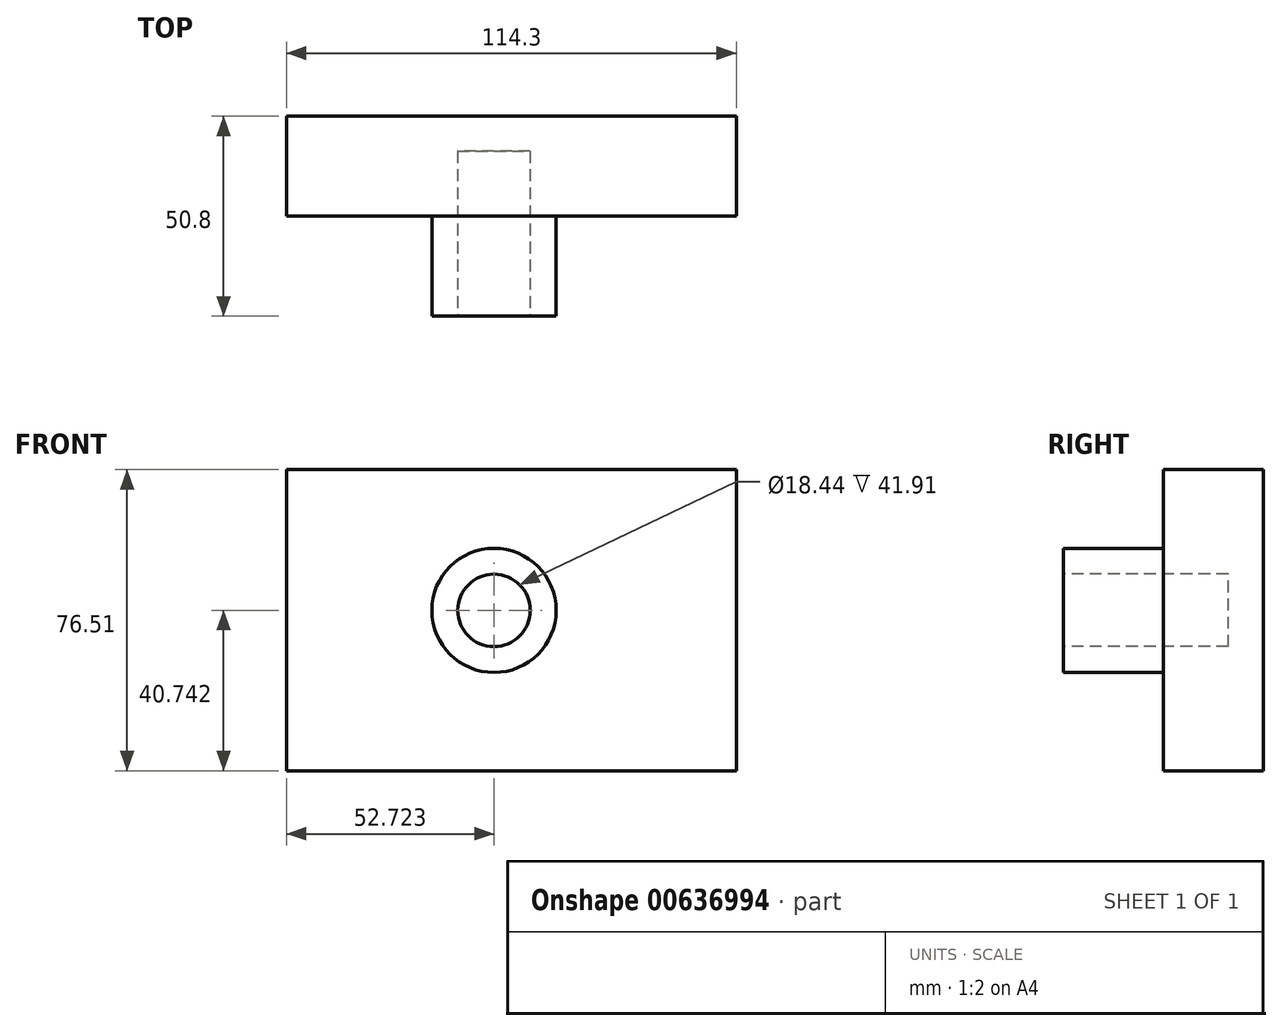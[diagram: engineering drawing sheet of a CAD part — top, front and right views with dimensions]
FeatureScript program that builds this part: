
annotation { "Feature Type Name" : "Feature", "Feature Type Description" : "" }
export const myFeature = defineFeature(function(context is Context, id is Id, definition is map)
    precondition{}
    {
        {
            var Q0;
            Q0=qCreatedBy(makeId("Front.planeOp"),FACE);
            var sketch = newSketch(context, id + "F0", { "sketchPlane" : qUnion([Q0])});
            skLineSegment(sketch, "E0", {"start": v(-42.86, 44.34) * mm, "end": v(-42.86, -32.17) * mm});
            skLineSegment(sketch, "E1", {"start": v(-42.86, -32.17) * mm, "end": v(71.44, -32.17) * mm});
            skLineSegment(sketch, "E2", {"start": v(71.44, -32.17) * mm, "end": v(71.44, 44.34) * mm});
            skLineSegment(sketch, "E3", {"start": v(71.44, 44.34) * mm, "end": v(-42.86, 44.34) * mm});
            skSolve(sketch);
        }
        {
            var Q0;
            Q0=makeQuery(id+"F0.imprint","IMPRINT",FACE,{"disambiguationData":[TD([[makeQuery(id+"F0.imprint","IMPRINT",EDGE,{"derivedFrom":sQuery(id+"F0.wireOp",EDGE,"E0")}),1.0]])]});
            extrude(context, id + "F1", {"entities" : qUnion([Q0]), "depth" : 25.4 * mm, "offsetDistance" : 25.4 * mm});
        }
        {
            var Q0;
            Q0=makeQuery(id+"F1.opExtrude","CAP_FACE",FACE,{"disambiguationData":[OSD([sQuery(id+"F0.wireOp",EDGE,"E0"),sQuery(id+"F0.wireOp",EDGE,"E1"),sQuery(id+"F0.wireOp",EDGE,"E2"),sQuery(id+"F0.wireOp",EDGE,"E3")])],"isStart":false});
            var sketch = newSketch(context, id + "F2", { "sketchPlane" : qUnion([Q0])});
            skCircle(sketch, "E4", {"center": v(9.86, 8.57) * mm, "radius": 15.78 * mm});
            skSolve(sketch);
        }
        {
            var Q0;
            Q0 = qSketchRegion(id + "F2", true);
            extrude(context, id + "F3", {"entities" : qUnion([Q0]), "operationType" : NewBodyOperationType.ADD, "depth" : 25.4 * mm, "offsetDistance" : 25.4 * mm});
        }
        {
            var Q0;
            Q0=makeQuery(id+"F3.opExtrude","CAP_FACE",FACE,{"disambiguationData":[OSD([sQuery(id+"F2.wireOp",EDGE,"E4")])],"isStart":false});
            var sketch = newSketch(context, id + "F4", { "sketchPlane" : qUnion([Q0])});
            skCircle(sketch, "E5", {"center": v(9.86, 8.57) * mm, "radius": 9.22 * mm});
            skSolve(sketch);
        }
        {
            var Q0;
            Q0 = qSketchRegion(id + "F4", true);
            extrude(context, id + "F5", {"entities" : qUnion([Q0]), "operationType" : NewBodyOperationType.REMOVE, "oppositeDirection" : true, "depth" : 41.9 * mm, "offsetDistance" : 25.4 * mm});
        }
    });
